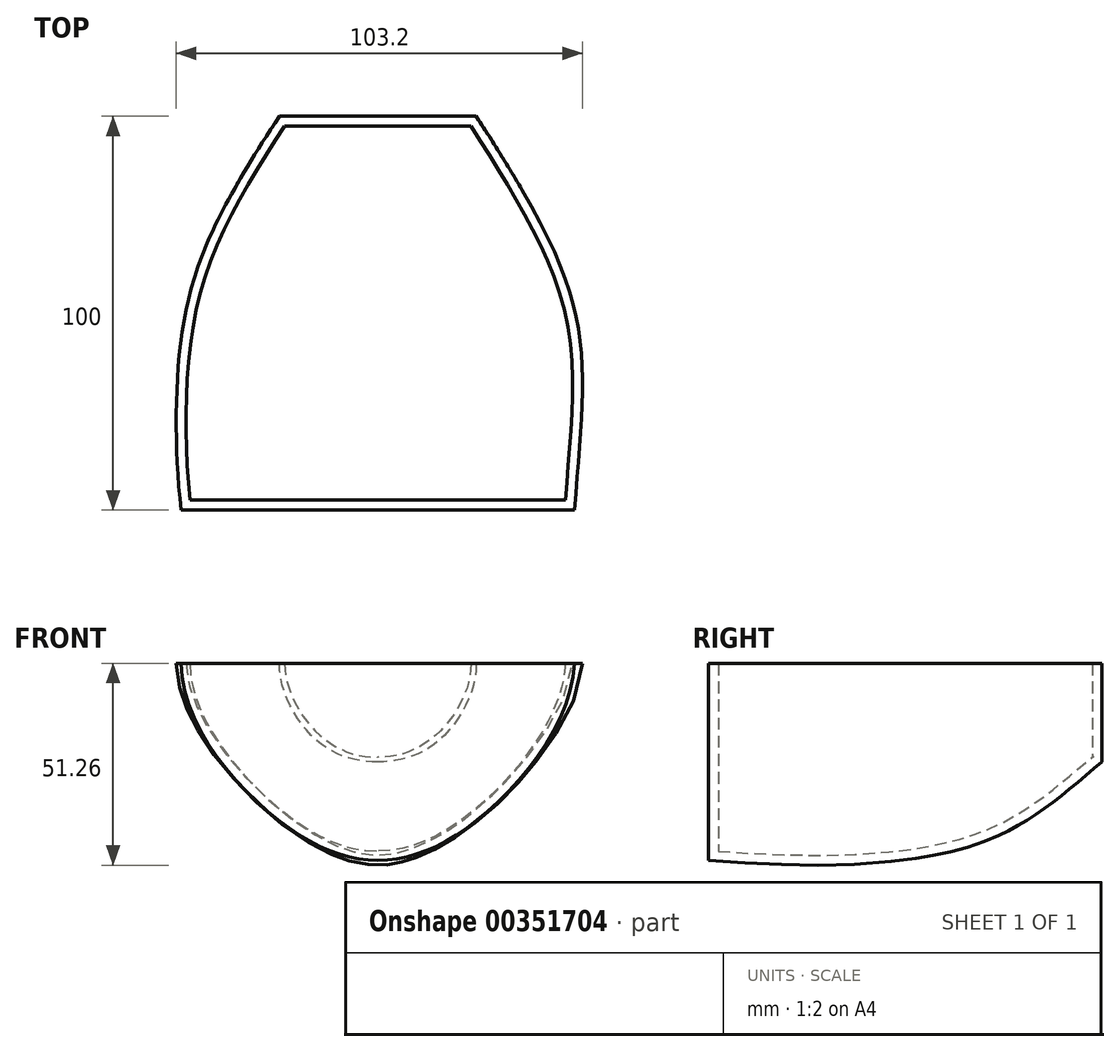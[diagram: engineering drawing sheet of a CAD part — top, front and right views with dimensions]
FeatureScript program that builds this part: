
annotation { "Feature Type Name" : "Feature", "Feature Type Description" : "" }
export const myFeature = defineFeature(function(context is Context, id is Id, definition is map)
    precondition{}
    {
        {
            var Q0;
            Q0=qCreatedBy(makeId("Front.planeOp"),FACE);
            cPlane(context, id + "F0", {"entities" : qUnion([Q0]), "cplaneType" : CPlaneType.OFFSET, "offset" : 100 * mm, "oppositeDirection" : true, "width" : 150 * mm, "height" : 150 * mm});
        }
        {
            var Q0;
            Q0=qCreatedBy(makeId("Front.planeOp"),FACE);
            var sketch = newSketch(context, id + "F1", { "sketchPlane" : qUnion([Q0])});
            skFitSpline(sketch, "E0", {"points": [v(-50, 0) * mm, v(-25, -40) * mm, v(0, -50) * mm, v(25, -40) * mm, v(50, 0) * mm], "startDerivative": vector(0.2, -158) * mm, "endDerivative": vector(7.74, 158) * mm});
            skLineSegment(sketch, "E1", {"start": v(-50, 0) * mm, "end": v(50, 0) * mm});
            skSolve(sketch);
        }
        {
            var Q0;
            Q0=qCreatedBy(id+"F0.planeOp",FACE);
            var sketch = newSketch(context, id + "F2", { "sketchPlane" : qUnion([Q0])});
            skFitSpline(sketch, "E2", {"points": [v(25, 0) * mm, v(15, -20) * mm, v(0, -25) * mm, v(-15, -20) * mm, v(-25, 0) * mm], "startDerivative": vector(1.29, -82.84) * mm, "endDerivative": vector(0.07, 82.84) * mm});
            skLineSegment(sketch, "E3", {"start": v(25, 0) * mm, "end": v(-25, 0) * mm});
            skSolve(sketch);
        }
        {
            var Q0;
            Q0=qCreatedBy(makeId("Right.planeOp"),FACE);
            var sketch = newSketch(context, id + "F3", { "sketchPlane" : qUnion([Q0])});
            skFitSpline(sketch, "E4", {"points": [v(100, -25) * mm, v(69.32, -45.52) * mm, v(0, -50) * mm], "startDerivative": vector(-58.47, -47.72) * mm, "endDerivative": vector(-119.85, 10.32) * mm});
            skSolve(sketch);
        }
        {
            var Q0;
            Q0=qCreatedBy(makeId("Top.planeOp"),FACE);
            var sketch = newSketch(context, id + "F4", { "sketchPlane" : qUnion([Q0])});
            skFitSpline(sketch, "E5", {"points": [v(-50, 0) * mm, v(-49.9, 43.67) * mm, v(-25, 100) * mm], "startDerivative": vector(-9.73, 93.3) * mm, "endDerivative": vector(96.76, 145.25) * mm});
            skFitSpline(sketch, "E6", {"points": [v(50, 0) * mm, v(51.3, 43.67) * mm, v(25, 100) * mm], "startDerivative": vector(8.22, 115.79) * mm, "endDerivative": vector(-96.6, 147.55) * mm});
            skSolve(sketch);
        }
        {
            var Q0;
            Q0=makeQuery(id+"F1.imprint","IMPRINT",FACE,{"disambiguationData":[TD([[makeQuery(id+"F1.imprint","IMPRINT",EDGE,{"derivedFrom":sQuery(id+"F1.wireOp",EDGE,"E0")}),1.0]])]});
            var Q1;
            Q1=makeQuery(id+"F2.imprint","IMPRINT",FACE,{"disambiguationData":[TD([[makeQuery(id+"F2.imprint","IMPRINT",EDGE,{"derivedFrom":sQuery(id+"F2.wireOp",EDGE,"E2")}),-1.0]])]});
            var Q2;
            Q2=sQuery(id+"F4.wireOp",EDGE,"E6");
            var Q3;
            Q3=sQuery(id+"F3.wireOp",EDGE,"E4");
            var Q4;
            Q4=sQuery(id+"F4.wireOp",EDGE,"E5");
            loft(context, id + "F5", {"addGuides" : true, "sheetProfilesArray" : [{ "sheetProfileEntities" : qUnion([Q0]) }, { "sheetProfileEntities" : qUnion([Q1]) }], "guidesArray" : [{ "guideEntities" : qUnion([Q2]), "guideDerivativeType" : LoftGuideDerivativeType.DEFAULT, "guideDerivativeMagnitude" : 1 }, { "guideEntities" : qUnion([Q3]), "guideDerivativeType" : LoftGuideDerivativeType.DEFAULT, "guideDerivativeMagnitude" : 1 }, { "guideEntities" : qUnion([Q4]), "guideDerivativeType" : LoftGuideDerivativeType.DEFAULT, "guideDerivativeMagnitude" : 1 }]});
        }
        {
            var Q0;
            Q0=makeQuery(id+"F5.opLoft","SWEPT_FACE",FACE,{"disambiguationData":[OSD([sQuery(id+"F1.wireOp",EDGE,"E1"),sQuery(id+"F2.wireOp",EDGE,"E2"),sQuery(id+"F2.wireOp",EDGE,"E3"),sQuery(id+"F4.wireOp",EDGE,"E5"),sQuery(id+"F4.wireOp",EDGE,"E6")])]});
            shell(context, id + "F6", {"entities" : qUnion([Q0]), "thickness" : 2.5 * mm});
        }
    });
